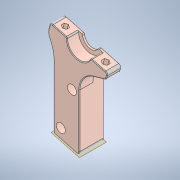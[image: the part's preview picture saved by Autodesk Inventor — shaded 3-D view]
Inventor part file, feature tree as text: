
AUTODESK INVENTOR PART (.ipt)
format: ipt  version: 2021.2 (Build 252289000, 289)  size: 400,384 bytes
history: native  units: mm
features: other x6, fillet x1, chamfer x1
ambient origin geometry x8: Origin, YZ Plane, XZ Plane, XY Plane, X Axis, Y Axis, Z Axis, Center Point
bodies: Body1 (feature_tree)
feature tree (8):
  other  "Твёрдое тело.ipt"
  other  "РабПлоскость1"
  other  "Разделение1"
  fillet  "Сопряжение1"  Radius=10.0mm
  chamfer  "Фаска1"  Distance=2.0mm
  other  "Ножка 1::Твёрдое тело.ipt"
  other  "Элемент создания тегов1"
  other  "Твердое тело1"
